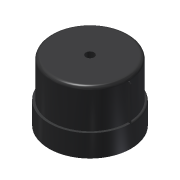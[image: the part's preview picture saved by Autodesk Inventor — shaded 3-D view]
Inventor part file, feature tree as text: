
AUTODESK INVENTOR PART (.ipt)
format: ipt  version: 2014 SP1 (Build 180222100, 222)  size: 151,552 bytes
history: native  units: in
note: dims shown in document units (in); Inventor stores cm internally (conversion verified against a paired STEP export)
features: extrude x5, sketch x5, chamfer x2, fillet x2
ambient origin geometry x8: Origin, YZ Plane, XZ Plane, XY Plane, X Axis, Y Axis, Z Axis, Center Point
bodies: Solid1 (feature_tree)
feature tree (14):
  extrude  "Extrusion1"  Depth=0.312in TaperAngle=0.0deg
  extrude  "Extrusion2"  Depth=0.55in TaperAngle=0.0deg
  extrude  "Extrusion3"  TaperAngle=180.0deg  [1 undecoded]
  chamfer  "Chamfer1"  Distance=0.5in
  chamfer  "Chamfer2"  Distance=0.02in Angle=45.0deg
  fillet  "Fillet1"  Radius=0.05in
  fillet  "Fillet2"  Radius=0.02in
  extrude  "Extrusion4"  Depth=1.0in TaperAngle=0.0deg
  extrude  "Extrusion5"  Depth=0.1181in
  sketch  "Sketch1"  dims[d0=1.16in d1=0.312in d2=0.0in]
  sketch  "Sketch2"  dims[d3=1.095in d4=0.55in d5=0.0in]
  sketch  "Sketch4"  dims[d7=180.0deg d8=180.0deg d9=0.5in d10=0.0in d11=0.02in d12=0.125in d13=45.0deg]
  sketch  "Sketch5"  dims[d14=0.02in d15=0.125in d16=45.0deg d17=0.05in d18=0.02in]
  sketch  "Sketch6"  dims[d19=0.625in d20=1.0in d21=0.0in d22=0.1181in d23=0.862in d24=0.0in]
note: 1 required parameter value undecoded (feature->parameter linkage not recoverable at this tier; creation-order binding heuristic only, values carry confidence <= 0.55)
